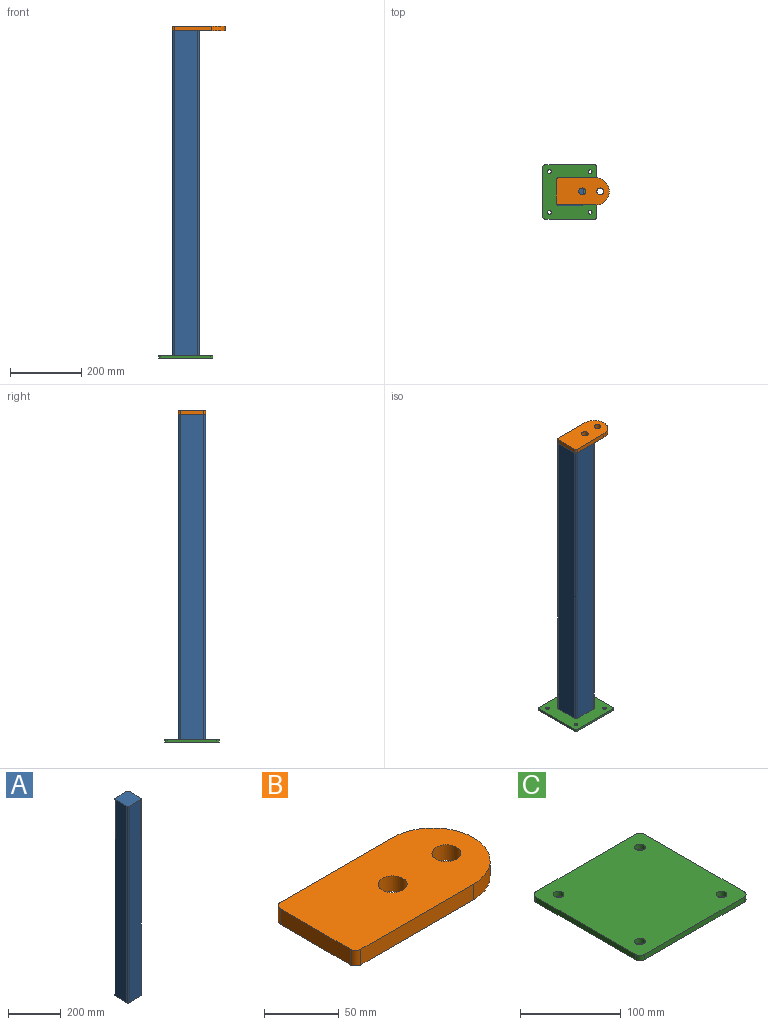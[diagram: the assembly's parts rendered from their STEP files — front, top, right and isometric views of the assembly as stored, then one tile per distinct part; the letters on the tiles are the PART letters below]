
ASSEMBLY  parts=3 mates=2
PART A: 10 faces, bbox 76.2x76.2x914.4 mm
  f0: plane 914.4x63.5mm, normal (0,1,0), area 58064.4mm2, adj f1,f7,f8,f9
  f1: cylinder r=6.35mm len=914.4mm, axis (0,0,-1), area 9120.7mm2, adj f0,f2,f8,f9
  f2: plane 914.4x63.5mm, normal (-1,0,0), area 58064.4mm2, adj f1,f3,f8,f9
  f3: cylinder r=6.35mm len=914.4mm, axis (0,0,-1), area 9120.7mm2, adj f2,f4,f8,f9
  f4: plane 914.4x63.5mm, normal (0,-1,0), area 58064.4mm2, adj f3,f5,f8,f9
  f5: cylinder r=6.35mm len=914.4mm, axis (0,0,-1), area 9120.7mm2, adj f4,f6,f8,f9
  f6: plane 914.4x63.5mm, normal (1,0,0), area 58064.4mm2, adj f5,f7,f8,f9
  f7: cylinder r=6.35mm len=914.4mm, axis (0,0,-1), area 9120.7mm2, adj f0,f6,f8,f9
  f8: plane 76.2x76.2mm, normal (0,0,1), area 5771.8mm2, adj f0,f1,f2,f3,f4,f5,f6,f7
  f9: plane 76.2x76.2mm, normal (0,0,-1), area 5771.8mm2, adj f0,f1,f2,f3,f4,f5,f6,f7
PART B: 10 faces, bbox 149.2x76.2x12.7 mm
  f0: plane 106.05x12.7mm, normal (0,1,0), area 1346.8mm2, adj f5,f6,f8,f9
  f1: plane 66.04x12.7mm, normal (-1,0,0), area 838.7mm2, adj f5,f6,f7,f9
  f2: cylinder r=9.65mm len=19.3mm, axis (0,0,-1), area 770.2mm2, adj f5,f6
  f3: cylinder r=9.65mm len=19.3mm, axis (0,0,-1), area 770.2mm2, adj f5,f6
  f4: plane 106.05x12.7mm, normal (0,-1,0), area 1346.8mm2, adj f5,f6,f7,f8
  f5: plane 149.23x76.2mm, normal (0,0,1), area 10151.5mm2, adj f0,f1,f2,f3,f4,f7,f8,f9
  f6: plane 149.23x76.2mm, normal (0,0,-1), area 10151.5mm2, adj f0,f1,f2,f3,f4,f7,f8,f9
  f7: cylinder r=5.08mm len=12.7mm, axis (0,0,1), area 101.3mm2, adj f1,f4,f5,f6
  f8: cylinder r=38.1mm len=76.2mm, axis (0,0,-1), area 1520.1mm2, adj f0,f4,f5,f6
  f9: cylinder r=5.08mm len=12.7mm, axis (0,0,-1), area 101.3mm2, adj f0,f1,f5,f6
PART C: 14 faces, bbox 152.4x152.4x6.4 mm
  f0: plane 139.7x6.35mm, normal (1,0,0), area 887.1mm2, adj f1,f7,f8,f9
  f1: cylinder r=6.35mm len=6.35mm, axis (0,0,-1), area 63.3mm2, adj f0,f2,f8,f9
  f2: plane 139.7x6.35mm, normal (0,1,0), area 887.1mm2, adj f1,f3,f8,f9
  f3: cylinder r=6.35mm len=6.35mm, axis (0,0,-1), area 63.3mm2, adj f2,f4,f8,f9
  f4: plane 139.7x6.35mm, normal (-1,0,0), area 887.1mm2, adj f3,f5,f8,f9
  f5: cylinder r=6.35mm len=6.35mm, axis (0,0,-1), area 63.3mm2, adj f4,f6,f8,f9
  f6: plane 139.7x6.35mm, normal (0,-1,0), area 887.1mm2, adj f5,f7,f8,f9
  f7: cylinder r=6.35mm len=6.35mm, axis (0,0,-1), area 63.3mm2, adj f0,f6,f8,f9
  f8: plane 152.4x152.4mm, normal (0,0,1), area 22825.1mm2, adj f0,f1,f2,f3,f4,f5,f6,f7
  f9: plane 152.4x152.4mm, normal (0,0,-1), area 22825.1mm2, adj f0,f1,f2,f3,f4,f5,f6,f7
  f10: cylinder r=5.4mm len=10.8mm, axis (0,0,1), area 215.4mm2, adj f8,f9
  f11: cylinder r=5.4mm len=10.8mm, axis (0,0,1), area 215.4mm2, adj f8,f9
  f12: cylinder r=5.4mm len=10.8mm, axis (0,0,1), area 215.4mm2, adj f8,f9
  f13: cylinder r=5.4mm len=10.8mm, axis (0,0,1), area 215.4mm2, adj f8,f9
PLACE A t=(-143.12,183.39,-148.32)mm
PLACE B t=(6.1,183.39,766.08)mm
PLACE C t=(-181.22,221.49,-154.67)mm
MATE fastened C.f8 <-> A.f9  axis (0,0,1) through (-105.02,145.29,-148.32)mm
MATE fastened B.f6 <-> A.f8  axis (0,0,-1) through (-143.12,145.29,766.08)mm
